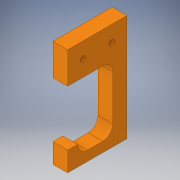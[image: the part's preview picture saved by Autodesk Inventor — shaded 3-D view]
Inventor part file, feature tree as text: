
AUTODESK INVENTOR PART (.ipt)
format: ipt  version: 2019 (Build 230136000, 136)  size: 140,288 bytes
history: native  units: in
note: dims shown in document units (in); Inventor stores cm internally (conversion verified against a paired STEP export)
features: sketch x2, extrude x1, hole x1, fillet x1, projected_geometry x1
ambient origin geometry x8: Origin, YZ Plane, XZ Plane, XY Plane, X Axis, Y Axis, Z Axis, Center Point
bodies: Body1 (feature_tree)
feature tree (6):
  extrude  "Extrusion2"  Depth=2.7in
  hole  "Hole1"  [1 undecoded]
  fillet  "Fillet2"  Radius=0.5in
  sketch  "Sketch1"  dims[d0=1.5in d1=2.7in]
  sketch  "Sketch2"  dims[d2=0.36in d3=0.25in d4=0.5in d5=0.25in d6=0.25in d10=0.8in d11=1.5in d12=0.37in d13=0.0in d14=0.725in d15=1.5in d16=0.3875in d17=0.8in d18=0.4in d19=0.4in d20=0.14in d21=0.75in d22=0.375in d23=0.25in d24=0.5635in d25=0.432in d26=0.8108in d27=0.25in]
  projected_geometry  "Projected Loop1"
note: 1 required parameter value undecoded (feature->parameter linkage not recoverable at this tier; creation-order binding heuristic only, values carry confidence <= 0.55)
